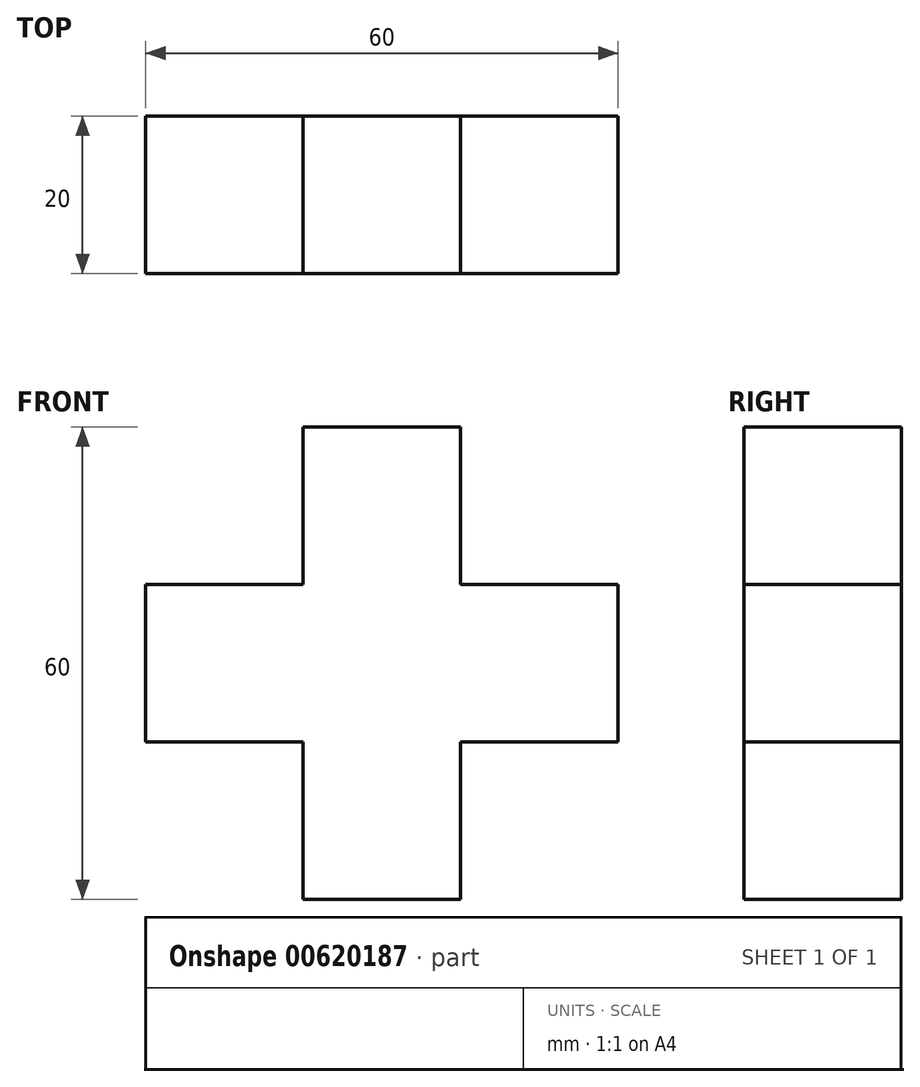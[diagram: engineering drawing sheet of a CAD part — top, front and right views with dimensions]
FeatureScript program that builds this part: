
annotation { "Feature Type Name" : "Feature", "Feature Type Description" : "" }
export const myFeature = defineFeature(function(context is Context, id is Id, definition is map)
    precondition{}
    {
        {
            var Q0;
            Q0=qCreatedBy(makeId("Front.planeOp"),FACE);
            var sketch = newSketch(context, id + "F0", { "sketchPlane" : qUnion([Q0])});
            skLineSegment(sketch, "E0", {"start": v(-50.18, 40.35) * mm, "end": v(-50.18, 20.35) * mm});
            skLineSegment(sketch, "E1", {"start": v(-50.18, 20.35) * mm, "end": v(-30.18, 20.35) * mm});
            skLineSegment(sketch, "E2", {"start": v(-30.18, 20.35) * mm, "end": v(-30.18, 0.35) * mm});
            skLineSegment(sketch, "E3", {"start": v(-30.18, 0.35) * mm, "end": v(-10.18, 0.35) * mm});
            skLineSegment(sketch, "E4", {"start": v(-10.18, 0.35) * mm, "end": v(-10.18, 20.35) * mm});
            skLineSegment(sketch, "E5", {"start": v(-10.18, 20.35) * mm, "end": v(9.82, 20.35) * mm});
            skLineSegment(sketch, "E6", {"start": v(9.82, 20.35) * mm, "end": v(9.82, 40.35) * mm});
            skLineSegment(sketch, "E7", {"start": v(9.82, 40.35) * mm, "end": v(-10.18, 40.35) * mm});
            skLineSegment(sketch, "E8", {"start": v(-10.18, 40.35) * mm, "end": v(-10.18, 60.35) * mm});
            skLineSegment(sketch, "E9", {"start": v(-10.18, 60.35) * mm, "end": v(-30.18, 60.35) * mm});
            skLineSegment(sketch, "E10", {"start": v(-30.18, 60.35) * mm, "end": v(-30.18, 40.35) * mm});
            skLineSegment(sketch, "E11", {"start": v(-30.18, 40.35) * mm, "end": v(-50.18, 40.35) * mm});
            skSolve(sketch);
        }
        {
            var Q0;
            Q0 = qSketchRegion(id + "F0", true);
            extrude(context, id + "F1", {"entities" : qUnion([Q0]), "depth" : 20 * mm, "offsetDistance" : 25 * mm});
        }
    });
